# Revit family: HD061-2016.04.29-BT-ScreenPanel G
name_source: partatom
category: Generic Models
revit_build: Autodesk Revit 2016 (Build: 20150714_1515(x64)
units: mm (PartAtom-declared; Revit-internal decimal feet)

## family parameters
Always vertical = Yes
Can host rebar = No
Cut with Voids When Loaded = No
Part Type = Normal
Room Calculation Point = No
Round Connector Dimension = Use Diameter
Shared = No
Work Plane-Based = No

## types (1)
- Productos HD
    BT_Alto = 481 modulo maximo
    BT_Ancho = 50 mm (espesor)
    BT_Codigo_Origen = HD061
    BT_Color = 100 colores
    BT_Descripcion = -El panel Screenpanel es un producto de una sola piel que permite revestir fachadas. Se puede instalar de forma vertical, horizontal o diagonal.<salto> -  Se cuenta con dos opciones de panel, con y sin cantería. Ambas alternativas se instalan directo a estructura mediante perfil de aluminio estándar (en el caso con cantería) o pernos (sin cantería).<salto> - El panel se presenta en tres modulaciones distintas: 300, 400 y 500 mm. Todas estas opciones están disponibles tanto para las opciones con y sin cantería. <salto>-  La principal particularidad de este panel es que en su alternativa perforada (sin cantería) se puede obtener, a través del perforado, distintos diseños y figuras. Esto gracias al uso de una máquina de control numérico, a la cual se le ingresa el diseño deseado en planos Cad, generando la figura a través de las perforaciones.
    BT_EETT = El panel deberá tener una geometría rectangular y plana, formado por 

un fleje tipo piel, plegado en todo su perímetro, con un espesor total 

de 50mm,

El panel es fabricado en aluzinc con un espesor de 1 ó 1,2mm

El avance útil del panel es de 481mm.

El esquema de pintura considera la aplicación de un primer poliéster 

de secado al horno por ambas caras, con un espesor de 5 ± 2 micras, 

y la aplicación de un esmalte de terminación poliéster secado al horno 

por ambas caras, con un espesor total de 25 ± 2 micras (incluido el 

primer).

La instalación del panel deberá ser vertical y considera el uso de una 

escuadra 50 x 50 en espesor 3mm galvanizada, mas un perfil Z de 

dimensiones 50 x 74mm en espesor 1,5mm y material aluzinc

Opciones de perforado estándar: #110M1 - #110M3 - #111 - #114 -

#115 - #116 - #401 - #402 - #403 - #150 - #151 - #405 - #406 -

#407 - #408 - #420
    BT_Elemento = Paneles y Revestimientos verticales
    BT_Especialidad = Arquitectura
    BT_Fabricante = Hunter Douglas
    BT_Itemizado_Estandar_CDT = D 01 08 04
    BT_Linea = A pedido
    BT_Marca = Hunter Douglas
    BT_MasterFormat® = 07 42 13
    BT_Material = AZ-AL-ACC
    BT_Nombre_Comercial = ScreenPanel G
    BT_Nombre_Corto = ScreenPanel G
    BT_Nombre_Tecnico = ScreenPanel G
    BT_Profundidad = 3500 mm (alto)
    BT_SKU = 003583
    BT_Uso = Exterior / Interior
    BT_Web_del_Producto = http://www.hunterdouglas.cl
    ID_Objeto = BT_F_F_334
    ID_Source = BIMTOOL
    Material = Metal

## geometry (parser evidence)
native form markers: Sweep x23
no freeform markers — native parametric forms only
